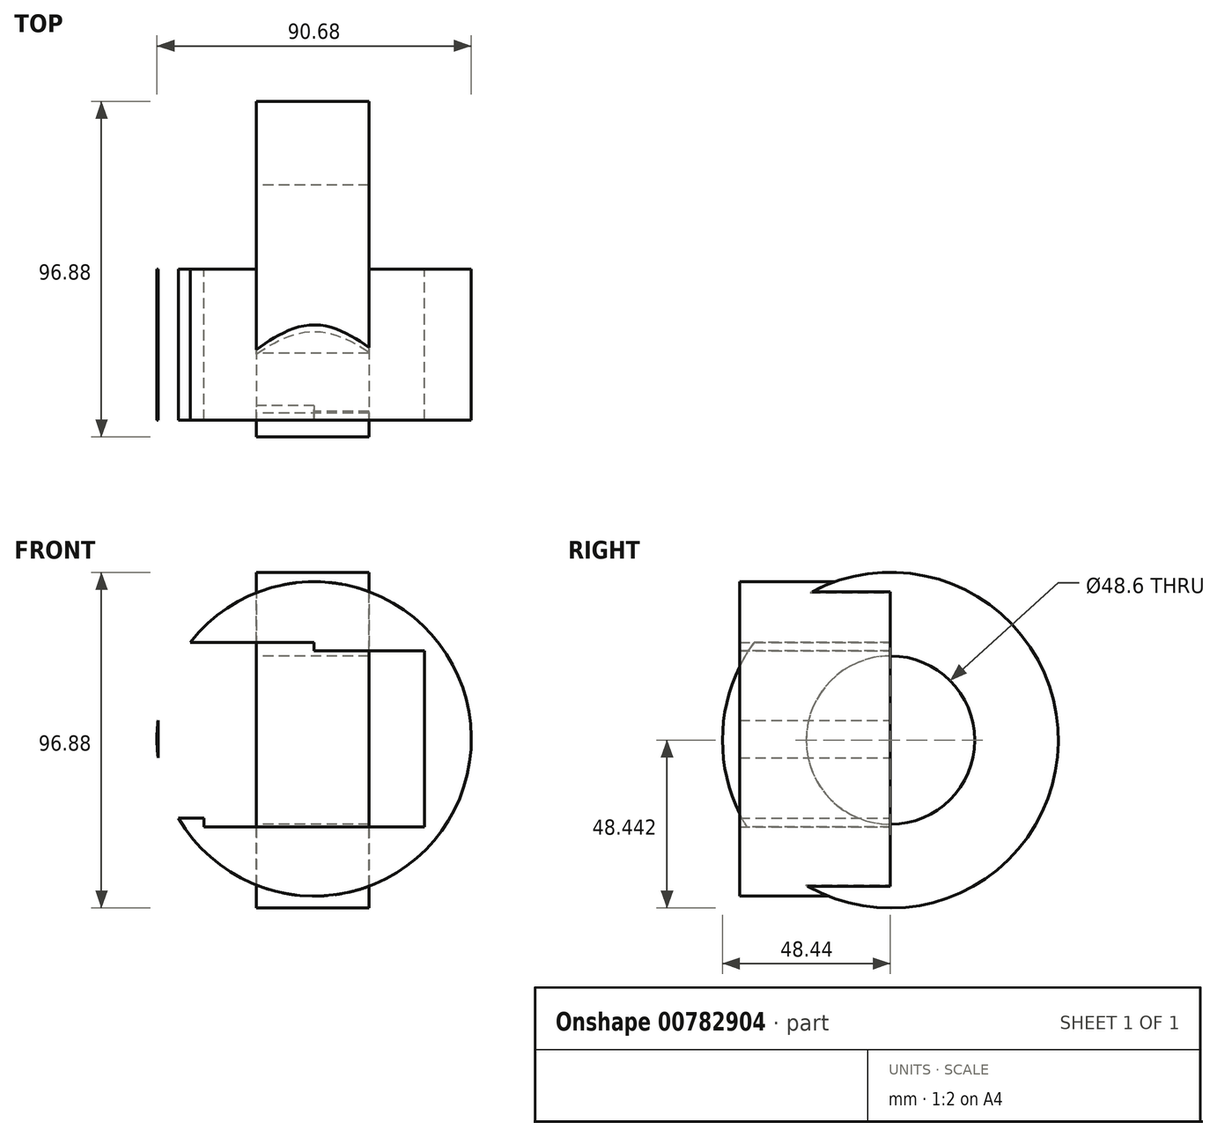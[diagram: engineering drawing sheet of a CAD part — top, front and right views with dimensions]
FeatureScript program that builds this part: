
annotation { "Feature Type Name" : "Feature", "Feature Type Description" : "" }
export const myFeature = defineFeature(function(context is Context, id is Id, definition is map)
    precondition{}
    {
        {
            var Q0;
            Q0=qCreatedBy(makeId("Front.planeOp"),FACE);
            var sketch = newSketch(context, id + "F0", { "sketchPlane" : qUnion([Q0])});
            skCircle(sketch, "E0", {"center": v(0, 0) * mm, "radius": 45.34 * mm});
            skLineSegment(sketch, "E1.bottom", {"start": v(31.85, -25.4) * mm, "end": v(-31.85, -25.4) * mm});
            skLineSegment(sketch, "E1.top", {"start": v(31.85, 25.4) * mm, "end": v(-31.85, 25.4) * mm});
            skLineSegment(sketch, "E1.left", {"start": v(31.85, -25.4) * mm, "end": v(31.85, 25.4) * mm});
            skLineSegment(sketch, "E1.right", {"start": v(-31.85, -25.4) * mm, "end": v(-31.85, 25.4) * mm});
            skSolve(sketch);
        }
        {
            var Q0;
            Q0 = qSketchRegion(id + "F0", true);
            extrude(context, id + "F1", {"entities" : qUnion([Q0]), "depth" : 43.54 * mm, "offsetDistance" : 25.4 * mm});
        }
        {
            var Q0;
            Q0=qCreatedBy(makeId("Right.planeOp"),FACE);
            var sketch = newSketch(context, id + "F2", { "sketchPlane" : qUnion([Q0])});
            skLineSegment(sketch, "E2.bottom", {"start": v(-56.78, 27.87) * mm, "end": v(18.21, 27.87) * mm});
            skLineSegment(sketch, "E2.top", {"start": v(-56.78, -22.85) * mm, "end": v(18.21, -22.85) * mm});
            skLineSegment(sketch, "E2.left", {"start": v(-56.78, 27.87) * mm, "end": v(-56.78, -22.85) * mm});
            skLineSegment(sketch, "E2.right", {"start": v(18.21, 27.87) * mm, "end": v(18.21, -22.85) * mm});
            skSolve(sketch);
        }
        {
            var Q0;
            Q0 = qSketchRegion(id + "F2", true);
            extrude(context, id + "F3", {"entities" : qUnion([Q0]), "operationType" : NewBodyOperationType.REMOVE, "oppositeDirection" : true, "depth" : 45.02 * mm, "offsetDistance" : 25.4 * mm});
        }
        {
            var Q0;
            Q0=qCreatedBy(makeId("Front.planeOp"),FACE);
            var sketch = newSketch(context, id + "F4", { "sketchPlane" : qUnion([Q0])});
            skLineSegment(sketch, "E3.bottom", {"start": v(-16.67, 48.08) * mm, "end": v(15.81, 48.08) * mm});
            skLineSegment(sketch, "E3.top", {"start": v(-16.67, 23.94) * mm, "end": v(15.81, 23.94) * mm});
            skLineSegment(sketch, "E3.left", {"start": v(-16.67, 48.08) * mm, "end": v(-16.67, 23.94) * mm});
            skLineSegment(sketch, "E3.right", {"start": v(15.81, 48.08) * mm, "end": v(15.81, 23.94) * mm});
            skLineSegment(sketch, "E4", {"start": v(62.42, -0.36) * mm, "end": v(15.76, -0.36) * mm, "construction": true});
            skSolve(sketch);
        }
        {
            var Q0;
            Q0=makeQuery(id+"F4.imprint","IMPRINT",FACE,{"disambiguationData":[TD([[makeQuery(id+"F4.imprint","IMPRINT",EDGE,{"derivedFrom":sQuery(id+"F4.wireOp",EDGE,"E3.bottom")}),-1.0]])]});
            var Q1;
            Q1=sQuery(id+"F4.wireOp",EDGE,"E4");
            revolve(context, id + "F5", {"operationType" : NewBodyOperationType.ADD, "surfaceOperationType" : NewSurfaceOperationType.NEW, "entities" : qUnion([Q0]), "axis" : qUnion([Q1]), "revolveType" : RevolveType.FULL, "oppositeDirection" : true});
        }
    });
